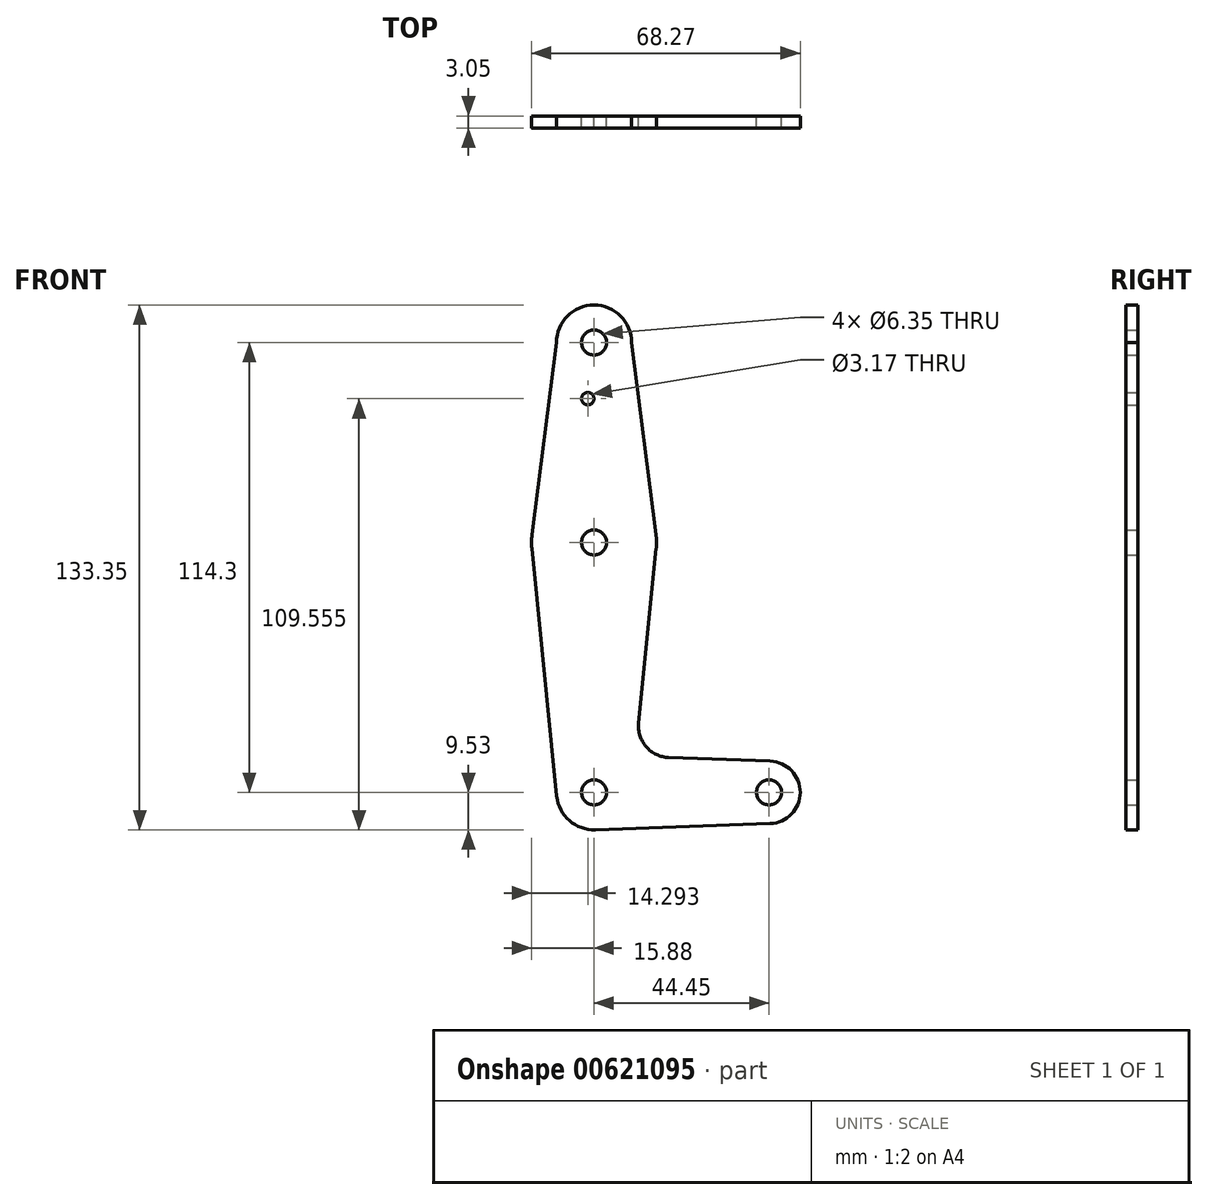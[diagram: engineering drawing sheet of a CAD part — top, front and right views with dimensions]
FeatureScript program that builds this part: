
annotation { "Feature Type Name" : "Feature", "Feature Type Description" : "" }
export const myFeature = defineFeature(function(context is Context, id is Id, definition is map)
    precondition{}
    {
        {
            var Q0;
            Q0=qCreatedBy(makeId("Front.planeOp"),FACE);
            var sketch = newSketch(context, id + "F0", { "sketchPlane" : qUnion([Q0])});
            skLineSegment(sketch, "E0", {"start": v(0, 50.8) * mm, "end": v(0, -63.5) * mm});
            skLineSegment(sketch, "E1", {"start": v(0, -63.5) * mm, "end": v(44.45, -63.5) * mm});
            skCircle(sketch, "E2", {"center": v(0, 50.8) * mm, "radius": 9.53 * mm});
            skCircle(sketch, "E3", {"center": v(0, -63.5) * mm, "radius": 9.53 * mm});
            skCircle(sketch, "E4", {"center": v(44.45, -63.5) * mm, "radius": 7.94 * mm});
            skCircle(sketch, "E5", {"center": v(0, 0) * mm, "radius": 15.88 * mm});
            skLineSegment(sketch, "E6", {"start": v(-9.53, 50.8) * mm, "end": v(-16, 0) * mm});
            skLineSegment(sketch, "E7", {"start": v(9.53, 50.8) * mm, "end": v(16, 0) * mm});
            skLineSegment(sketch, "E8", {"start": v(-15.8, -1.59) * mm, "end": v(-9.48, -64.45) * mm});
            skLineSegment(sketch, "E9", {"start": v(15.8, -1.59) * mm, "end": v(11.34, -45.91) * mm});
            skLineSegment(sketch, "E10", {"start": v(18.97, -54.65) * mm, "end": v(44.73, -55.57) * mm});
            skLineSegment(sketch, "E11", {"start": v(44.73, -71.43) * mm, "end": v(0, -73.03) * mm});
            skCircle(sketch, "E12", {"center": v(0, 50.8) * mm, "radius": 3.18 * mm});
            skCircle(sketch, "E13", {"center": v(0, 0) * mm, "radius": 3.18 * mm});
            skCircle(sketch, "E14", {"center": v(0, -63.5) * mm, "radius": 3.18 * mm});
            skCircle(sketch, "E15", {"center": v(44.45, -63.5) * mm, "radius": 3.18 * mm});
            skCircle(sketch, "E16", {"center": v(-1.59, 36.53) * mm, "radius": 1.59 * mm});
            skArc(sketch, "E17.filletArc", {"start": v(11.34, -45.91) * mm, "mid": v(13.26, -51.93) * mm, "end": v(18.97, -54.65) * mm});
            skSolve(sketch);
        }
        {
            var Q0;
            Q0 = qSketchRegion(id + "F0", true);
            extrude(context, id + "F1", {"entities" : qUnion([Q0]), "depth" : 3.05 * mm, "offsetDistance" : 25.4 * mm});
        }
        {
            var Q0;
            {var subQ0=sQuery(id+"F0.wireOp",EDGE,"E3");var subQ1=sQuery(id+"F0.wireOp",EDGE,"E0");var subQ2=makeQuery(id+"F0.imprint","INTERSECT",VERTEX,{"derivedFrom":[subQ1,subQ0]});Q0=makeQuery(id+"F0.imprint","IMPRINT",FACE,{"disambiguationData":[TD([[makeQuery(id+"F0.imprint","IMPRINT",EDGE,{"disambiguationData":[TD([[subQ2,-1.0]])],"derivedFrom":subQ1}),1.0]])]});}
            extrude(context, id + "F2", {"entities" : qUnion([Q0]), "operationType" : NewBodyOperationType.ADD, "depth" : 3.05 * mm, "offsetDistance" : 25.4 * mm});
        }
    });
